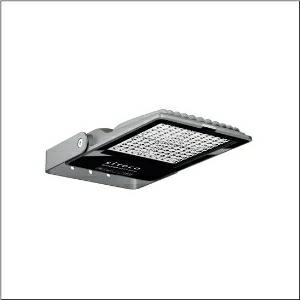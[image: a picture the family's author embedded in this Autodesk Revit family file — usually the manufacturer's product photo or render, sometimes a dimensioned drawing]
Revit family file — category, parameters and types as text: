
# Revit family: sicompact_r__31_mini___pl32_5xa7571c1k23_a489
name_source: partatom
category: Lighting Fixtures
units: mm (PartAtom-declared; Revit-internal decimal feet)

## family parameters
Cut with Voids When Loaded = No
Host = Face
Light Source = No
Part Type = Normal
Room Calculation Point = No
Round Connector Dimension = Use Diameter
Shared = No

## types (1)
- SiCompact® 31 mini  PL32 (1 x LED, 15000 lm, 100 W, 3000K)
    Apparent Load = 100 VA
    CIE Flux Codes = 32 69 98 100 100
    Color Rendering = 70
    Color Temperature = 3000K
    Default Elevation = 1800 mm
    Description = SiCompact® 31 mini, floodlight, primary light control with lens, of plastic, of toughened safety glass, transparent, light distribution: PL32, light emission: direct distribution, primary light characteristic: asymmetric, installation type: surface-mounted, LED, High Power LED, rated luminous flux: 15.000lm, luminous efficacy: 150lm/W, light colour: 730, colour temperature: 3000K, control gear: ON/OFF, with cable, 3x 1.5mm², mains connection: 220..240V, AC, 50/60Hz, connection cable pre-assembled, cable length: 2m, rated input power: 100W, of diecast aluminium, specular, metallic grey (RAL 9006), length: 461mm, width: 261mm, height: 62mm, bracket, of sheet steel, coated, metallic grey (RAL 9006), ON/OFF, protection rating (complete): IP66, insulation class (complete): insulation class I (protective earthing), certification: CE, ENEC, impact resistance: IK08, permissible operating ambient temperature: -40..+45°C, packaging unit: 1 piece

Light Distribution: PL32
    Height = 62 mm  [stored 0.203412 ft]
    Lamp = 1 x LED
    Lamp Light Flux = 15000 lm
    Lamp Power = 100 W
    Lamp count = 1
    Length = 460 mm
    Luminous efficacy = 150 lm/W
    Manufacturer = Siteco
    ModVariant = No
    Model = 5XA7571C1K23
    Mounting Place = Wall
    Mounting Type = Surface mounted
    Number of Poles = 1
    OnlyDefault = Yes
    Power Factor = 1
    Product Name = SiCompact® 31 mini | PL32
    Product group = floodlight | wall mounted
    ProductGroupID = 2001
    Protection Class = Protection class I
    Protection Degree = IP 66
    RLX_Detail_Level = 1
    RLX_Emergency_Light_Flux = 0 lm
    RLX_Emergency_Type = 0
    RLX_Emergency_Type_DB = No
    RlxData = <blob elided: 126661 chars, md5=8c7ff6e2>
    Socket = socket
    Standby Power = 0 W
    System Light Flux = 15000 lm
    System Power = 100 W
    Type Comments = Product without accessories
    Type Image = l_1006951.jpg
    URL = http://relux.com
    VarID = ---
    Voltage = 0 V
    Weight = 0.00 kg
    Width = 260 mm

note: [stored X ft] marks values corroborated as IEEE doubles in the binary element streams (Revit-internal decimal feet)

## geometry (parser evidence)
native form markers: Blend x4, Sweep x14
no freeform markers — native parametric forms only
